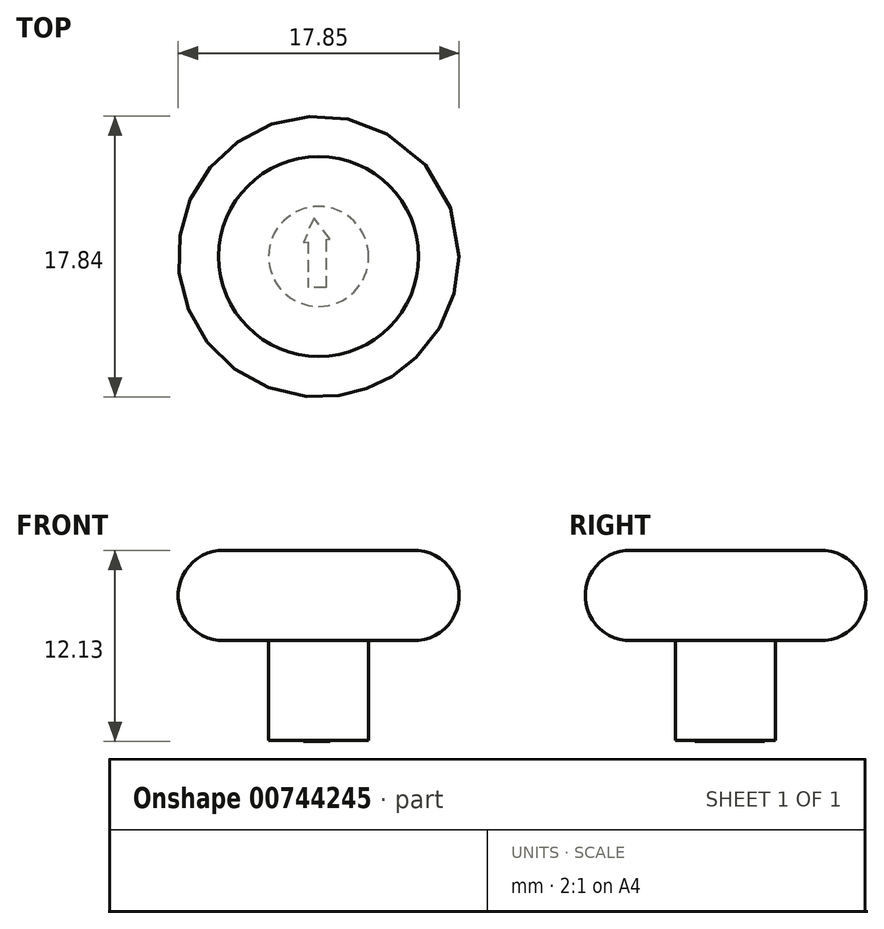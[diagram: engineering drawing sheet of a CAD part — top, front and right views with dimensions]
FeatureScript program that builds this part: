
annotation { "Feature Type Name" : "Feature", "Feature Type Description" : "" }
export const myFeature = defineFeature(function(context is Context, id is Id, definition is map)
    precondition{}
    {
        {
            var Q0;
            Q0=qCreatedBy(makeId("Front.planeOp"),FACE);
            var sketch = newSketch(context, id + "F0", { "sketchPlane" : qUnion([Q0])});
            skLineSegment(sketch, "E0.bottom", {"start": v(-39.6, 29.42) * mm, "end": v(-30.07, 29.42) * mm});
            skLineSegment(sketch, "E0.top", {"start": v(-39.6, 23.07) * mm, "end": v(-30.07, 23.07) * mm});
            skLineSegment(sketch, "E0.left", {"start": v(-39.6, 29.42) * mm, "end": v(-39.6, 23.07) * mm});
            skLineSegment(sketch, "E0.right", {"start": v(-30.07, 29.42) * mm, "end": v(-30.07, 23.07) * mm});
            skArc(sketch, "E1", {"start": v(-36.42, 28.79) * mm, "mid": v(-39, 25.93) * mm, "end": v(-36.42, 23.07) * mm});
            skLineSegment(sketch, "E2", {"start": v(-36.42, 28.79) * mm, "end": v(-30.07, 28.79) * mm});
            skSolve(sketch);
        }
        {
            var Q0;
            {var subQ3=sQuery(id+"F0.wireOp",EDGE,"E1");Q0=makeQuery(id+"F0.imprint","IMPRINT",FACE,{"disambiguationData":[TD([[makeQuery(id+"F0.imprint","IMPRINT",EDGE,{"derivedFrom":subQ3}),1.0]])]});}
            var Q1;
            Q1=sQuery(id+"F0.wireOp",EDGE,"E0.right");
            revolve(context, id + "F1", {"surfaceOperationType" : NewSurfaceOperationType.NEW, "entities" : qUnion([Q0]), "axis" : qUnion([Q1]), "revolveType" : RevolveType.FULL});
        }
        {
            var Q0;
            Q0=makeQuery(id+"F1.opRevolve","SWEPT_FACE",FACE,{"disambiguationData":[OSD([sQuery(id+"F0.wireOp",EDGE,"E0.top")])]});
            var sketch = newSketch(context, id + "F2", { "sketchPlane" : qUnion([Q0])});
            skCircle(sketch, "E3", {"center": v(-30.07, 0) * mm, "radius": 3.18 * mm});
            skSolve(sketch);
        }
        {
            var Q0;
            Q0=makeQuery(id+"F2.imprint","IMPRINT",FACE,{"disambiguationData":[TD([[makeQuery(id+"F2.imprint","IMPRINT",EDGE,{"derivedFrom":sQuery(id+"F2.wireOp",EDGE,"E3")}),1.0]])]});
            extrude(context, id + "F3", {"entities" : qUnion([Q0]), "operationType" : NewBodyOperationType.ADD, "depth" : 6.35 * mm, "offsetDistance" : 25.4 * mm});
        }
        {
            var Q0;
            Q0=makeQuery(id+"F3.opExtrude","CAP_FACE",FACE,{"disambiguationData":[OSD([sQuery(id+"F2.wireOp",EDGE,"E3")])],"isStart":false});
            var sketch = newSketch(context, id + "F4", { "sketchPlane" : qUnion([Q0])});
            skLineSegment(sketch, "E4.bottom", {"start": v(-29.62, -1.25) * mm, "end": v(-30.77, -1.25) * mm});
            skLineSegment(sketch, "E4.top", {"start": v(-29.62, 1.96) * mm, "end": v(-30.77, 1.96) * mm});
            skLineSegment(sketch, "E4.left", {"start": v(-29.62, -1.25) * mm, "end": v(-29.62, 1.96) * mm});
            skLineSegment(sketch, "E4.right", {"start": v(-30.77, -1.25) * mm, "end": v(-30.77, 1.96) * mm});
            skCircle(sketch, "E5.cCircle", {"center": v(-30.26, -1.48) * mm, "radius": 0.98 * mm, "construction": true});
            skLineSegment(sketch, "E5.0", {"start": v(-30.38, -2.45) * mm, "end": v(-31.04, -0.9) * mm});
            skLineSegment(sketch, "E5.1", {"start": v(-31.04, -0.9) * mm, "end": v(-29.36, -1.1) * mm});
            skLineSegment(sketch, "E5.2", {"start": v(-29.36, -1.1) * mm, "end": v(-30.38, -2.45) * mm});
            skSolve(sketch);
        }
        {
            var Q0;
            {var subQ0=sQuery(id+"F4.wireOp",EDGE,"E4.top");Q0=makeQuery(id+"F4.imprint","IMPRINT",FACE,{"disambiguationData":[TD([[makeQuery(id+"F4.imprint","IMPRINT",EDGE,{"derivedFrom":subQ0}),1.0]])]});}
            var Q1;
            {var subQ0=sQuery(id+"F4.wireOp",EDGE,"E4.bottom");Q1=makeQuery(id+"F4.imprint","IMPRINT",FACE,{"disambiguationData":[TD([[makeQuery(id+"F4.imprint","IMPRINT",EDGE,{"derivedFrom":subQ0}),-1.0]])]});}
            var Q2;
            {var subQ2=sQuery(id+"F4.wireOp",EDGE,"E4.bottom");Q2=makeQuery(id+"F4.imprint","IMPRINT",FACE,{"disambiguationData":[TD([[makeQuery(id+"F4.imprint","IMPRINT",EDGE,{"derivedFrom":subQ2}),1.0]])]});}
            extrude(context, id + "F5", {"entities" : qUnion([Q0, Q1, Q2]), "operationType" : NewBodyOperationType.ADD, "depth" : 0.06 * mm, "offsetDistance" : 25.4 * mm});
        }
    });
